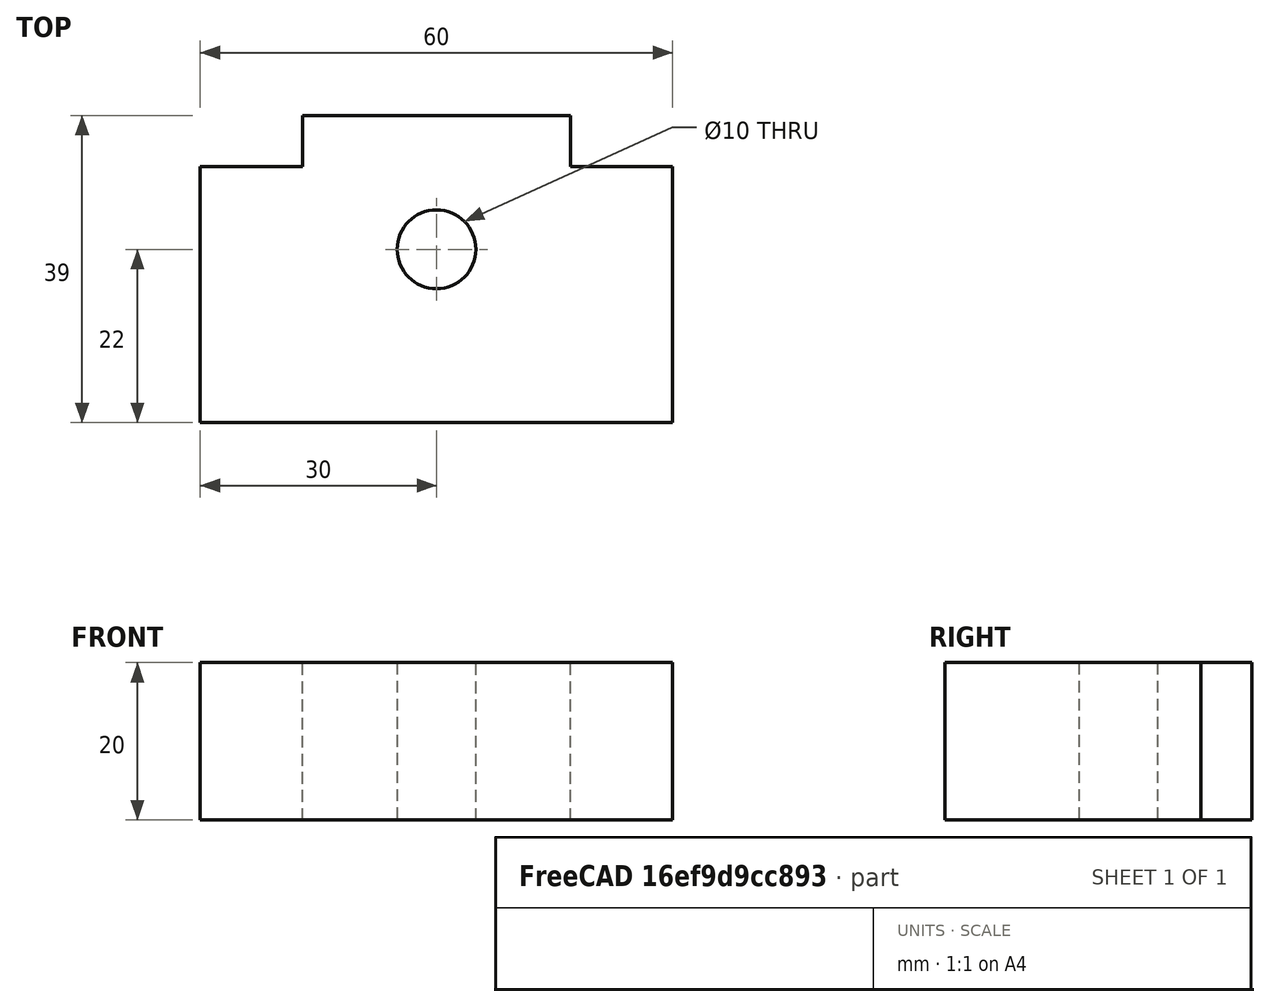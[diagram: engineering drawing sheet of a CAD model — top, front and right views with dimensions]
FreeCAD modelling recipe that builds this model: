
FCSTD DOCUMENT  (FreeCAD 0.21R33771 (Git))
Label: SupportoSingoloViteRicircolo12
License: All rights reserved
LicenseURL: http://en.wikipedia.org/wiki/All_rights_reserved
objects: Sketcher::SketchObject×2, PartDesign::Pad×1, PartDesign::CoordinateSystem×1, PartDesign::Body×1, App::MeasureDistance×1
note: 6 computed .brp shape members not serialized (recipe doc carries the construction recipe); baked Part::Feature solids carry a one-line shape summary decoded from their .brp

FEATURE [Sketcher::SketchObject] Sketch
  FullyConstrained = true
  MapMode = 5
  Support = -> [XY_Plane]
  sketch-geometry (9):
    g0: LineSegment StartX=-30 StartY=0 StartZ=0 EndX=30 EndY=0 EndZ=0
    g1: LineSegment StartX=30 StartY=0 StartZ=0 EndX=30 EndY=32.5 EndZ=0
    g2: LineSegment StartX=30 StartY=32.5 StartZ=0 EndX=17 EndY=32.5 EndZ=0
    g3: LineSegment StartX=17 StartY=32.5 StartZ=0 EndX=17 EndY=39 EndZ=0
    g4: LineSegment StartX=17 StartY=39 StartZ=0 EndX=-17 EndY=39 EndZ=0
    g5: LineSegment StartX=-17 StartY=39 StartZ=0 EndX=-17 EndY=32.5 EndZ=0
    g6: LineSegment StartX=-17 StartY=32.5 StartZ=0 EndX=-30 EndY=32.5 EndZ=0
    g7: LineSegment StartX=-30 StartY=32.5 StartZ=0 EndX=-30 EndY=0 EndZ=0
    g8: Circle CenterX=0 CenterY=22 CenterZ=0 NormalX=0 NormalY=0 NormalZ=1 AngleXU=0 Radius=5
  constraints (25):
    c: PointOnObject(g0,g-1)
    c: Coincident(g1,g0)
    c: Vertical(g1)
    c: Coincident(g2,g1)
    c: Horizontal(g2)
    c: Coincident(g3,g2)
    c: Vertical(g3)
    c: Coincident(g5,g4)
    c: Vertical(g5)
    c: Coincident(g6,g5)
    c: Coincident(g7,g6)
    c: Coincident(g7,g0)
    c: Vertical(g7)
    c: DistanceX(g0,g0) = 60
    c: DistanceX(g4,g4) = 34
    c: Coincident(g3,g4)
    c: Symmetric(g0,g0,g-2)
    c: Symmetric(g4,g3,g-2)
    c: Horizontal(g6)
    c: Equal(g7,g1)
    c: DistanceY(g7,g7) = 32.5
    c: DistanceY(g0,g3) = 39
    c: PointOnObject(g8,g-2)
    c: DistanceY(g-1,g8) = 22
    c: Radius(g8) = 5
FEATURE [PartDesign::Pad] Pad
  Direction = (0,0,1)
  Length = 20
  Length2 = 10
  Profile = -> Sketch
  ReferenceAxis = -> Sketch [N_Axis]
  Type = 0
FEATURE [Sketcher::SketchObject] Sketch001
  FullyConstrained = false
  MapMode = 5
  Placement = pos=(0,32.5,0) rot=(0,0.707107,0.707107;3.14159rad)
  Support = -> [Pad]
  sketch-geometry (3):
    g0: LineSegment StartX=-37.1467 StartY=10 StartZ=0 EndX=33.8264 EndY=10 EndZ=0
    g1: Circle CenterX=-23 CenterY=10 CenterZ=0 NormalX=0 NormalY=0 NormalZ=1 AngleXU=0 Radius=3
    g2: Circle CenterX=23 CenterY=10 CenterZ=0 NormalX=0 NormalY=0 NormalZ=1 AngleXU=0 Radius=3
  constraints (7):
    c: Horizontal(g0)
    c: DistanceY(g-1,g0) = 10
    c: PointOnObject(g1,g0)
    c: Radius(g1) = 3
    c: Equal(g1,g2)
    c: Symmetric(g1,g2,g-2)
    c: DistanceX(g1,g2) = 46
FEATURE [PartDesign::CoordinateSystem] LCS_SupportoSingleVietericircolo12
  AttacherType = Attacher::AttachEngine3D
  MapMode = 11
  Placement = pos=(0,22,20) rot=(0,0,1;1.5708rad)
  Support = -> [Pad]
FEATURE [PartDesign::Body] Body
  Group = -> [Sketch,Pad,Sketch001,LCS_SupportoSingleVietericircolo12]
  Origin = -> Origin
  Tip = -> Pad
FEATURE [App::MeasureDistance] Distance  label="Distance: 60,00 mm"
  Distance = 60
  P1 = (-30,0,20)
  P2 = (30,0,20)
